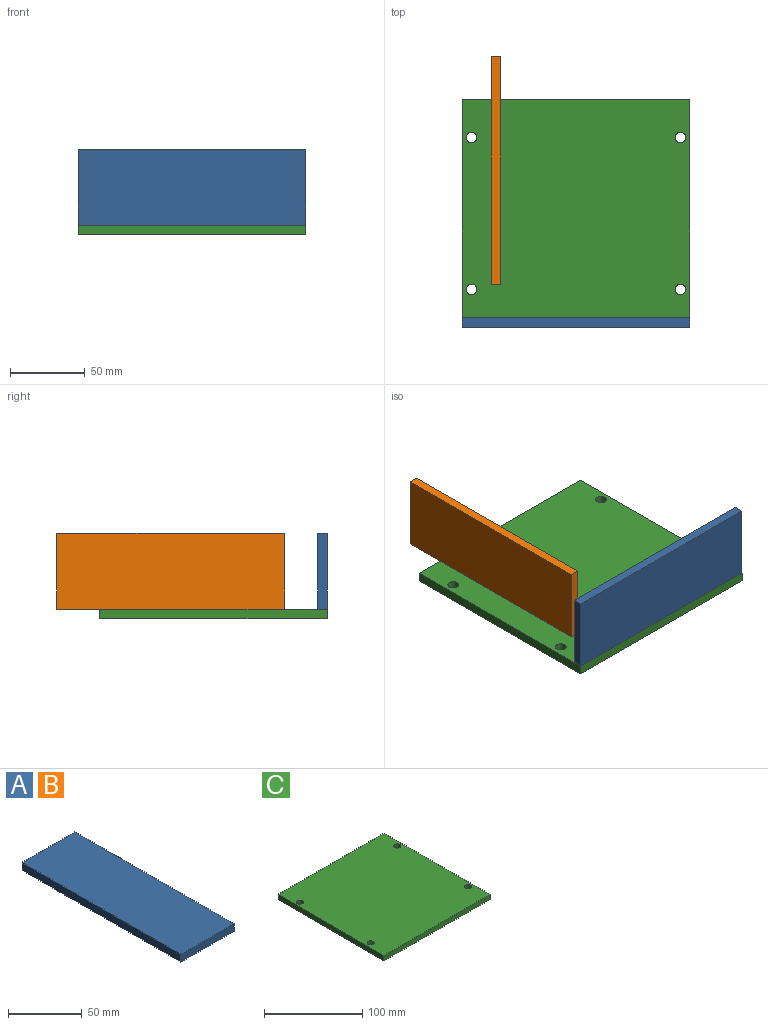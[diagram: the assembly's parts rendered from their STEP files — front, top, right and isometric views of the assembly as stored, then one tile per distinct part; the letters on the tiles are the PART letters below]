
ASSEMBLY  parts=3 mates=4
PART A: 6 faces, bbox 50.8x152.4x6.4 mm
  f0: plane 50.8x6.35mm, normal (0,1,0), area 322.6mm2, adj f1,f3,f4,f5
  f1: plane 152.4x6.35mm, normal (-1,0,0), area 967.7mm2, adj f0,f2,f4,f5
  f2: plane 50.8x6.35mm, normal (0,-1,0), area 322.6mm2, adj f1,f3,f4,f5
  f3: plane 152.4x6.35mm, normal (1,0,0), area 967.7mm2, adj f0,f2,f4,f5
  f4: plane 152.4x50.8mm, normal (0,0,1), area 7741.9mm2, adj f0,f1,f2,f3
  f5: plane 152.4x50.8mm, normal (0,0,-1), area 7741.9mm2, adj f0,f1,f2,f3
PART B: same geometry as A
PART C: 10 faces, bbox 152.4x152.4x6.4 mm
  f0: plane 152.4x6.35mm, normal (1,0,0), area 967.7mm2, adj f1,f3,f4,f5
  f1: plane 152.4x6.35mm, normal (0,1,0), area 967.7mm2, adj f0,f2,f4,f5
  f2: plane 152.4x6.35mm, normal (-1,0,0), area 967.7mm2, adj f1,f3,f4,f5
  f3: plane 152.4x6.35mm, normal (0,-1,0), area 967.7mm2, adj f0,f2,f4,f5
  f4: plane 152.4x152.4mm, normal (0,0,1), area 23065.4mm2, adj f0,f1,f2,f3,f6,f7,f8,f9
  f5: plane 152.4x152.4mm, normal (0,0,-1), area 23065.4mm2, adj f0,f1,f2,f3,f6,f7,f8,f9
  f6: cylinder r=3.57mm len=7.14mm, axis (0,0,1), area 142.5mm2, adj f4,f5
  f7: cylinder r=3.57mm len=7.14mm, axis (0,0,1), area 142.5mm2, adj f4,f5
  f8: cylinder r=3.57mm len=7.14mm, axis (0,0,1), area 142.5mm2, adj f4,f5
  f9: cylinder r=3.57mm len=7.14mm, axis (0,0,1), area 142.5mm2, adj f4,f5
PLACE A rot(axis=(0.58,0.58,-0.58),120deg) t=(-14.32,-132.52,59.68)mm
PLACE B rot(axis=(-0.71,0,0.71),180deg) t=(-64.81,-34.08,59.68)mm
PLACE C t=(-14.32,-62.67,27.93)mm fixed
MATE planar C.f0 <-> A.f0  axis (1,0,0) through (61.88,-62.67,31.11)mm
MATE planar A.f4 <-> C.f3  axis (0,-1,0) through (-14.32,-138.87,59.68)mm
MATE planar C.f4 <-> B.f3  axis (0,0,1) through (-14.32,-62.67,34.28)mm
MATE planar A.f3 <-> C.f4  axis (0,0,-1) through (-14.32,-135.7,34.28)mm
